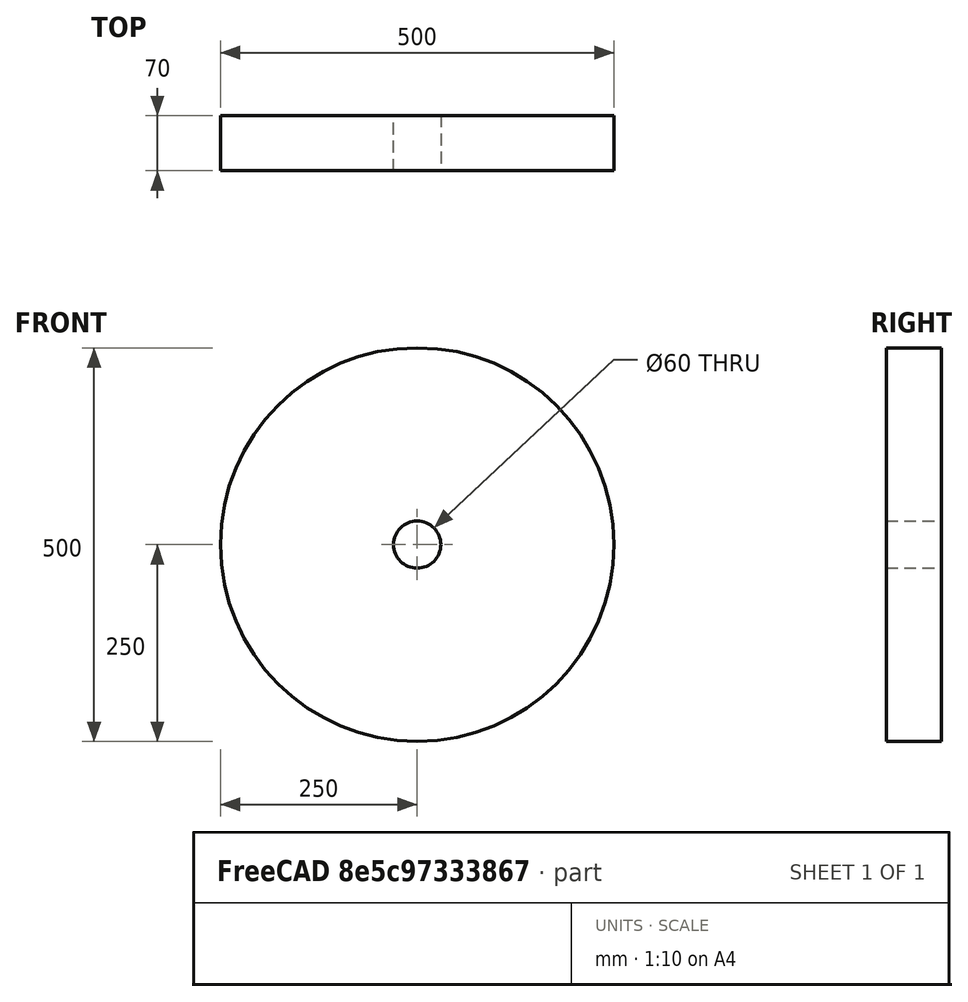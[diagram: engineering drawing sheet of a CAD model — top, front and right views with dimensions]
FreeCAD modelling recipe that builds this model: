
FCSTD DOCUMENT  (FreeCAD 0.20R29177 +426 (Git))
Label: wheel
License: All rights reserved
LicenseURL: http://en.wikipedia.org/wiki/All_rights_reserved
objects: Sketcher::SketchObject×1, PartDesign::Pad×1, PartDesign::Body×1
note: 4 computed .brp shape members not serialized (recipe doc carries the construction recipe); baked Part::Feature solids carry a one-line shape summary decoded from their .brp

FEATURE [Sketcher::SketchObject] Sketch
  FullyConstrained = true
  MapMode = 5
  Placement = pos=(0,0,0) rot=(1,0,0;1.5708rad)
  Support = -> [XZ_Plane]
  sketch-geometry (2):
    g0: Circle CenterX=0 CenterY=0 CenterZ=0 NormalX=0 NormalY=0 NormalZ=1 AngleXU=0 Radius=250
    g1: Circle CenterX=0 CenterY=0 CenterZ=0 NormalX=0 NormalY=0 NormalZ=1 AngleXU=0 Radius=30
  constraints (4):
    c: Coincident(g0,g-1)
    c: Coincident(g1,g0)
    c: Radius(g1) = 30
    c: Diameter(g0) = 500
FEATURE [PartDesign::Pad] Pad
  Direction = (0,-1,-2e-16)
  Length = 70
  Length2 = 10
  Placement = pos=(0,0,0) rot=(1,0,0;1.5708rad)
  Profile = -> Sketch
  ReferenceAxis = -> Sketch [N_Axis]
  Refine = true
  Type = 0
FEATURE [PartDesign::Body] Body
  Group = -> [Sketch,Pad]
  Origin = -> Origin
  Tip = -> Pad
